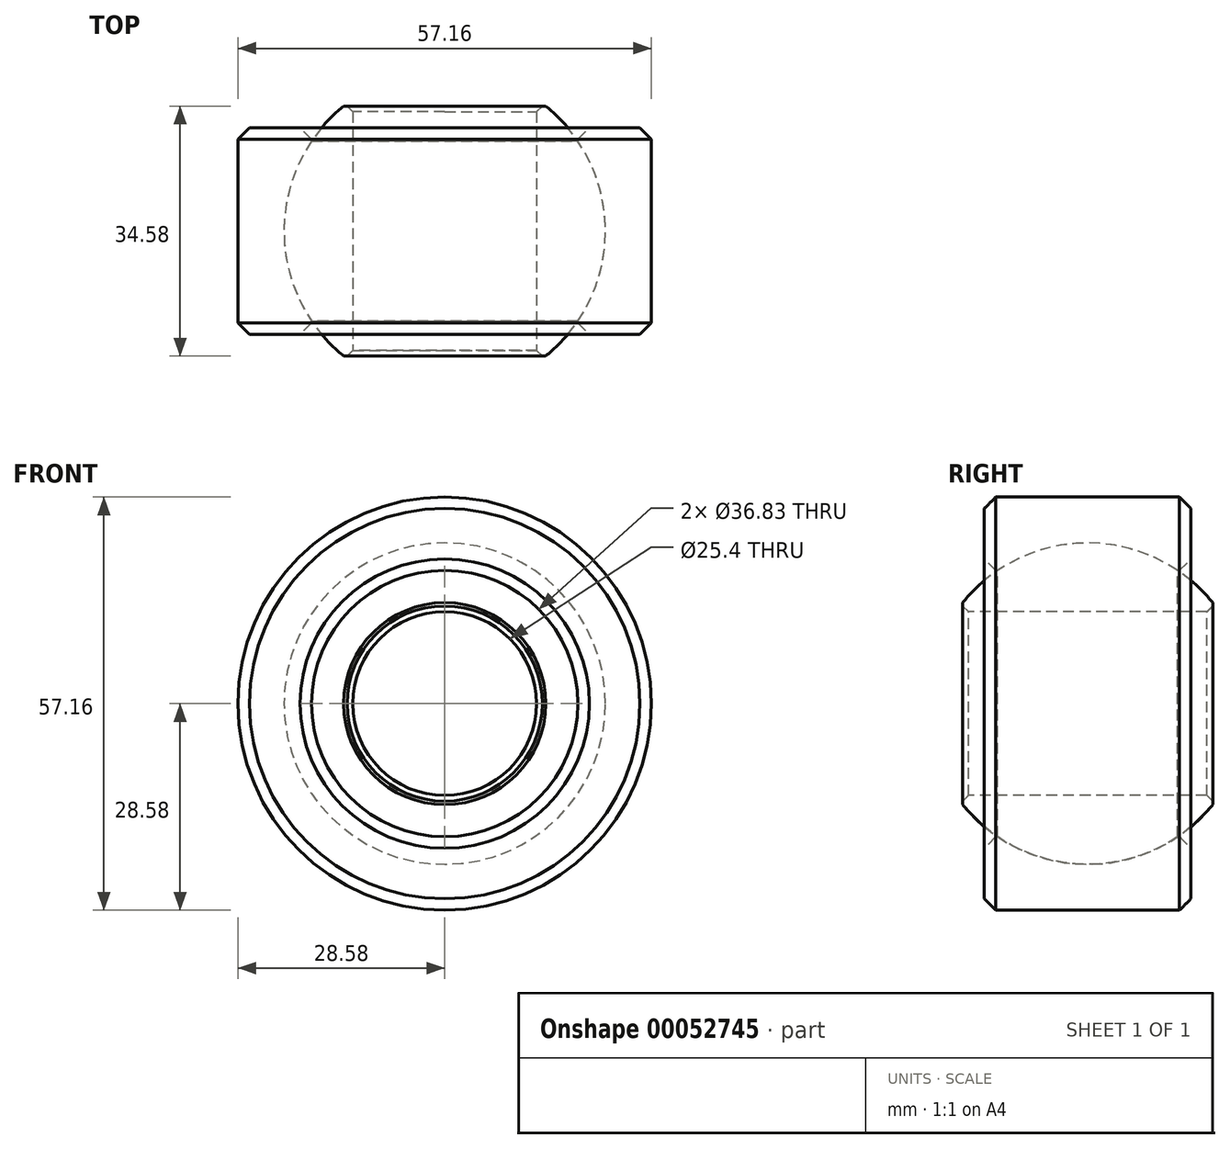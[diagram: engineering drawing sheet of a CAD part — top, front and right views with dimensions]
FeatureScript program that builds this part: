
annotation { "Feature Type Name" : "Feature", "Feature Type Description" : "" }
export const myFeature = defineFeature(function(context is Context, id is Id, definition is map)
    precondition{}
    {
        {
            var Q0;
            Q0=qCreatedBy(makeId("Top.planeOp"),FACE);
            var sketch = newSketch(context, id + "F0", { "sketchPlane" : qUnion([Q0])});
            skArc(sketch, "E0", {"start": v(13.97, -17.29) * mm, "mid": v(22.23, 0) * mm, "end": v(13.97, 17.29) * mm});
            skLineSegment(sketch, "E1", {"start": v(13.97, -17.29) * mm, "end": v(13.97, 17.29) * mm, "construction": true});
            skLineSegment(sketch, "E2", {"start": v(13.97, 17.29) * mm, "end": v(12.7, 17.29) * mm});
            skLineSegment(sketch, "E3", {"start": v(12.7, 17.29) * mm, "end": v(12.7, -17.29) * mm});
            skLineSegment(sketch, "E4", {"start": v(12.7, -17.29) * mm, "end": v(13.97, -17.29) * mm});
            skSolve(sketch);
        }
        {
            var Q0;
            Q0=qCreatedBy(makeId("Right.planeOp"),FACE);
            var sketch = newSketch(context, id + "F1", { "sketchPlane" : qUnion([Q0])});
            skLineSegment(sketch, "E5", {"start": v(0, 0) * mm, "end": v(81.4, 0) * mm, "construction": true});
            skSolve(sketch);
        }
        {
            var Q0;
            Q0 = qSketchRegion(id + "F0", true);
            var Q1;
            Q1=sQuery(id+"F1.wireOp",EDGE,"E5");
            revolve(context, id + "F2", {"entities" : qUnion([Q0]), "axis" : qUnion([Q1]), "revolveType" : RevolveType.FULL});
        }
        {
            var Q0;
            Q0=qCreatedBy(makeId("Top.planeOp"),FACE);
            var sketch = newSketch(context, id + "F3", { "sketchPlane" : qUnion([Q0])});
            skLineSegment(sketch, "E6", {"start": v(18.41, 14.29) * mm, "end": v(28.57, 14.29) * mm});
            skLineSegment(sketch, "E7", {"start": v(28.57, 14.29) * mm, "end": v(28.58, -14.29) * mm});
            skLineSegment(sketch, "E8", {"start": v(28.58, -14.29) * mm, "end": v(18.42, -14.29) * mm});
            skArc(sketch, "E9", {"start": v(18.42, -12.44) * mm, "mid": v(22.23, 0) * mm, "end": v(18.41, 12.44) * mm});
            skLineSegment(sketch, "E10", {"start": v(0, 0) * mm, "end": v(71.72, 0) * mm, "construction": true});
            skLineSegment(sketch, "E11", {"start": v(18.42, -14.29) * mm, "end": v(18.42, -12.44) * mm});
            skLineSegment(sketch, "E12.trimOffspring", {"start": v(18.41, 12.44) * mm, "end": v(18.41, 14.29) * mm});
            skSolve(sketch);
        }
        {
            var Q0;
            Q0 = qSketchRegion(id + "F3", true);
            var Q1;
            Q1=sQuery(id+"F1.wireOp",EDGE,"E5");
            revolve(context, id + "F4", {"entities" : qUnion([Q0]), "axis" : qUnion([Q1]), "revolveType" : RevolveType.FULL});
        }
        {
            var Q0;
            Q0=makeQuery(id+"F4.opRevolve","SWEPT_EDGE",EDGE,{"disambiguationData":[OSD([sQuery(id+"F3.wireOp",EDGE,"E6"),sQuery(id+"F3.wireOp",EDGE,"E7")])]});
            var Q1;
            Q1=makeQuery(id+"F4.opRevolve","SWEPT_EDGE",EDGE,{"disambiguationData":[OSD([sQuery(id+"F3.wireOp",EDGE,"E7"),sQuery(id+"F3.wireOp",EDGE,"E8")])]});
            chamfer(context, id + "F5", {"entities" : qUnion([Q0, Q1]), "width" : 1.59 * mm, "tangentPropagation" : true});
        }
        {
            var Q0;
            Q0=makeQuery(id+"F2.opRevolve","SWEPT_EDGE",EDGE,{"disambiguationData":[OSD([sQuery(id+"F0.wireOp",EDGE,"E2"),sQuery(id+"F0.wireOp",EDGE,"E3")])]});
            var Q1;
            Q1=makeQuery(id+"F2.opRevolve","SWEPT_EDGE",EDGE,{"disambiguationData":[OSD([sQuery(id+"F0.wireOp",EDGE,"E3"),sQuery(id+"F0.wireOp",EDGE,"E4")])]});
            chamfer(context, id + "F6", {"entities" : qUnion([Q0, Q1]), "width" : 0.8 * mm, "tangentPropagation" : true});
        }
        {
            var Q0;
            Q0=makeQuery(id+"F4.opRevolve","SWEPT_EDGE",EDGE,{"disambiguationData":[OSD([sQuery(id+"F3.wireOp",EDGE,"E8"),sQuery(id+"F3.wireOp",EDGE,"E11")])]});
            var Q1;
            Q1=makeQuery(id+"F4.opRevolve","SWEPT_EDGE",EDGE,{"disambiguationData":[OSD([sQuery(id+"F3.wireOp",EDGE,"E6"),sQuery(id+"F3.wireOp",EDGE,"E12.trimOffspring")])]});
            chamfer(context, id + "F7", {"entities" : qUnion([Q0, Q1]), "width" : 1.59 * mm, "tangentPropagation" : true});
        }
    });
